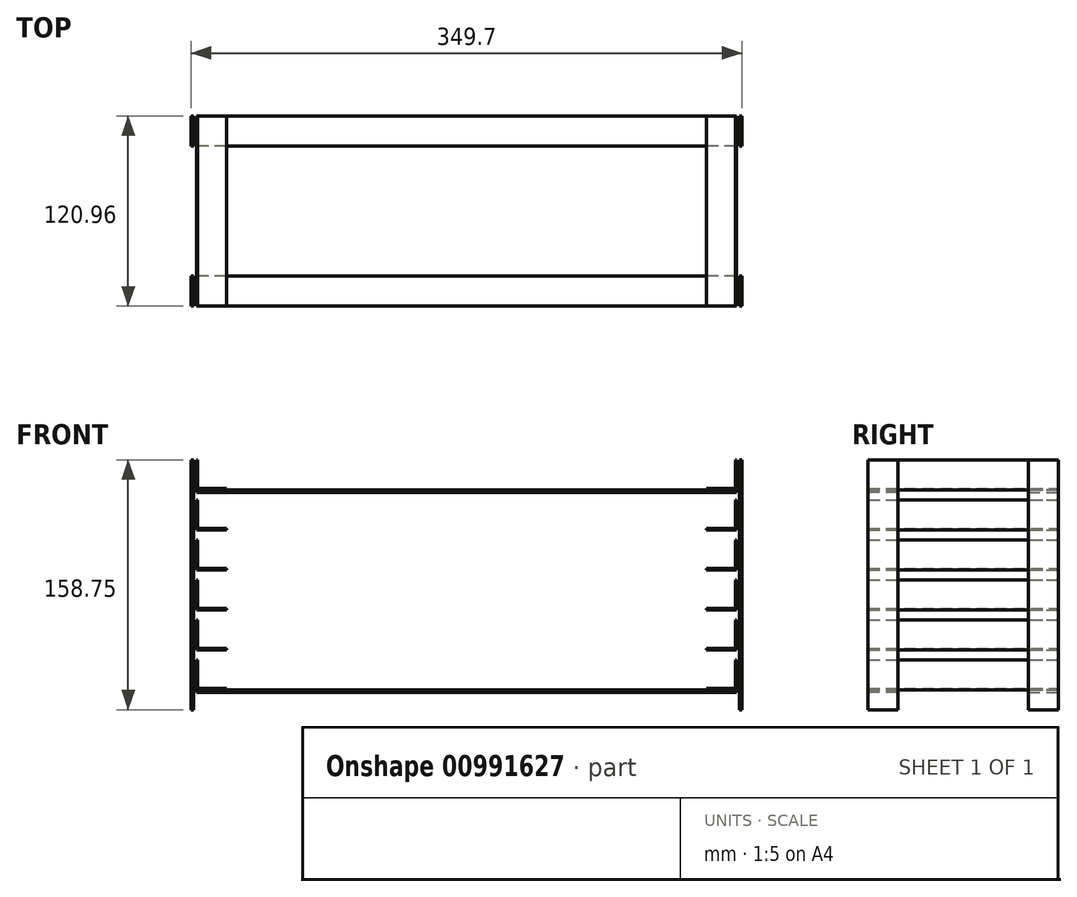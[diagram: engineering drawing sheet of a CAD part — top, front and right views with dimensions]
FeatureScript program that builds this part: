
annotation { "Feature Type Name" : "Feature", "Feature Type Description" : "" }
export const myFeature = defineFeature(function(context is Context, id is Id, definition is map)
    precondition{}
    {
        {
            var Q0;
            Q0=qCreatedBy(makeId("Front.planeOp"),FACE);
            var sketch = newSketch(context, id + "F0", { "sketchPlane" : qUnion([Q0])});
            skLineSegment(sketch, "E0", {"start": v(-171.45, 19.05) * mm, "end": v(-171.45, 0) * mm});
            skLineSegment(sketch, "E1", {"start": v(-171.45, 0) * mm, "end": v(-152.4, 0) * mm});
            skLineSegment(sketch, "E2", {"start": v(-152.4, 0) * mm, "end": v(-152.4, 0.76) * mm});
            skLineSegment(sketch, "E3", {"start": v(-152.4, 0.76) * mm, "end": v(-170.69, 0.76) * mm});
            skLineSegment(sketch, "E4", {"start": v(-171.45, 19.05) * mm, "end": v(-170.69, 19.05) * mm});
            skLineSegment(sketch, "E5", {"start": v(-170.69, 19.05) * mm, "end": v(-170.69, 0.76) * mm});
            skLineSegment(sketch, "E6.MirrorCS", {"start": v(152.4, 0.76) * mm, "end": v(170.69, 0.76) * mm});
            skLineSegment(sketch, "E7.MirrorCS", {"start": v(171.45, 0) * mm, "end": v(152.4, 0) * mm});
            skLineSegment(sketch, "E8.MirrorCS", {"start": v(170.69, 19.05) * mm, "end": v(170.69, 0.76) * mm});
            skLineSegment(sketch, "E9.MirrorCS", {"start": v(171.45, 19.05) * mm, "end": v(171.45, 0) * mm});
            skLineSegment(sketch, "E10.MirrorCS", {"start": v(171.45, 19.05) * mm, "end": v(170.69, 19.05) * mm});
            skLineSegment(sketch, "E11.MirrorCS", {"start": v(152.4, 0) * mm, "end": v(152.4, 0.76) * mm});
            skSolve(sketch);
        }
        {
            var Q0;
            Q0 = qSketchRegion(id + "F0", true);
            extrude(context, id + "F1", {"entities" : qUnion([Q0]), "endBound" : BoundingType.SYMMETRIC, "depth" : 120.65 * mm, "offsetDistance" : 25.4 * mm});
        }
        {
            var Q0;
            Q0=makeQuery(id+"F1.opExtrude","SWEPT_BODY",BODY,{"disambiguationData":[OSD([sQuery(id+"F0.wireOp",EDGE,"E0"),sQuery(id+"F0.wireOp",EDGE,"E1"),sQuery(id+"F0.wireOp",EDGE,"E2"),sQuery(id+"F0.wireOp",EDGE,"E3"),sQuery(id+"F0.wireOp",EDGE,"E4"),sQuery(id+"F0.wireOp",EDGE,"E5")])]});
            transform(context, id + "F2", {"entities" : qUnion([Q0]), "transformType" : TransformType.TRANSLATION_3D, "dx" : 0 * mm, "dy" : 0 * mm, "dz" : -25.4 * mm, "makeCopy" : true});
        }
        {
            var Q0;
            Q0=makeQuery(id+"F2.opPattern","COPY",BODY,{"derivedFrom":makeQuery(id+"F1.opExtrude","SWEPT_BODY",BODY,{"disambiguationData":[OSD([sQuery(id+"F0.wireOp",EDGE,"E0"),sQuery(id+"F0.wireOp",EDGE,"E1"),sQuery(id+"F0.wireOp",EDGE,"E2"),sQuery(id+"F0.wireOp",EDGE,"E3"),sQuery(id+"F0.wireOp",EDGE,"E4"),sQuery(id+"F0.wireOp",EDGE,"E5")])]}),"instanceName":"1"});
            transform(context, id + "F3", {"entities" : qUnion([Q0]), "transformType" : TransformType.TRANSLATION_3D, "dx" : 0 * mm, "dy" : 0 * mm, "dz" : -25.4 * mm, "makeCopy" : true});
        }
        {
            var Q0;
            Q0=makeQuery(id+"F3.opPattern","COPY",BODY,{"derivedFrom":makeQuery(id+"F2.opPattern","COPY",BODY,{"derivedFrom":makeQuery(id+"F1.opExtrude","SWEPT_BODY",BODY,{"disambiguationData":[OSD([sQuery(id+"F0.wireOp",EDGE,"E0"),sQuery(id+"F0.wireOp",EDGE,"E1"),sQuery(id+"F0.wireOp",EDGE,"E2"),sQuery(id+"F0.wireOp",EDGE,"E3"),sQuery(id+"F0.wireOp",EDGE,"E4"),sQuery(id+"F0.wireOp",EDGE,"E5")])]}),"instanceName":"1"}),"instanceName":"1"});
            transform(context, id + "F4", {"entities" : qUnion([Q0]), "transformType" : TransformType.TRANSLATION_3D, "dx" : 0 * mm, "dy" : 0 * mm, "dz" : -25.4 * mm, "makeCopy" : true});
        }
        {
            var Q0;
            Q0=makeQuery(id+"F4.opPattern","COPY",BODY,{"derivedFrom":makeQuery(id+"F3.opPattern","COPY",BODY,{"derivedFrom":makeQuery(id+"F2.opPattern","COPY",BODY,{"derivedFrom":makeQuery(id+"F1.opExtrude","SWEPT_BODY",BODY,{"disambiguationData":[OSD([sQuery(id+"F0.wireOp",EDGE,"E0"),sQuery(id+"F0.wireOp",EDGE,"E1"),sQuery(id+"F0.wireOp",EDGE,"E2"),sQuery(id+"F0.wireOp",EDGE,"E3"),sQuery(id+"F0.wireOp",EDGE,"E4"),sQuery(id+"F0.wireOp",EDGE,"E5")])]}),"instanceName":"1"}),"instanceName":"1"}),"instanceName":"1"});
            transform(context, id + "F5", {"entities" : qUnion([Q0]), "transformType" : TransformType.TRANSLATION_3D, "dx" : 0 * mm, "dy" : 0 * mm, "dz" : -25.4 * mm, "makeCopy" : true});
        }
        {
            var Q0;
            Q0=makeQuery(id+"F5.opPattern","COPY",BODY,{"derivedFrom":makeQuery(id+"F4.opPattern","COPY",BODY,{"derivedFrom":makeQuery(id+"F3.opPattern","COPY",BODY,{"derivedFrom":makeQuery(id+"F2.opPattern","COPY",BODY,{"derivedFrom":makeQuery(id+"F1.opExtrude","SWEPT_BODY",BODY,{"disambiguationData":[OSD([sQuery(id+"F0.wireOp",EDGE,"E0"),sQuery(id+"F0.wireOp",EDGE,"E1"),sQuery(id+"F0.wireOp",EDGE,"E2"),sQuery(id+"F0.wireOp",EDGE,"E3"),sQuery(id+"F0.wireOp",EDGE,"E4"),sQuery(id+"F0.wireOp",EDGE,"E5")])]}),"instanceName":"1"}),"instanceName":"1"}),"instanceName":"1"}),"instanceName":"1"});
            transform(context, id + "F6", {"entities" : qUnion([Q0]), "transformType" : TransformType.TRANSLATION_3D, "dx" : 0 * mm, "dy" : 0 * mm, "dz" : -25.4 * mm, "makeCopy" : true});
        }
        {
            var Q0;
            Q0=makeQuery(id+"F1.opExtrude","SWEPT_BODY",BODY,{"disambiguationData":[OSD([sQuery(id+"F0.wireOp",EDGE,"E6.MirrorCS"),sQuery(id+"F0.wireOp",EDGE,"E8.MirrorCS"),sQuery(id+"F0.wireOp",EDGE,"E7.MirrorCS"),sQuery(id+"F0.wireOp",EDGE,"E9.MirrorCS"),sQuery(id+"F0.wireOp",EDGE,"E10.MirrorCS"),sQuery(id+"F0.wireOp",EDGE,"E11.MirrorCS")])]});
            transform(context, id + "F7", {"entities" : qUnion([Q0]), "transformType" : TransformType.TRANSLATION_3D, "dx" : 0 * mm, "dy" : 0 * mm, "dz" : -25.4 * mm, "makeCopy" : true});
        }
        {
            var Q0;
            Q0=makeQuery(id+"F7.opPattern","COPY",BODY,{"derivedFrom":makeQuery(id+"F1.opExtrude","SWEPT_BODY",BODY,{"disambiguationData":[OSD([sQuery(id+"F0.wireOp",EDGE,"E6.MirrorCS"),sQuery(id+"F0.wireOp",EDGE,"E8.MirrorCS"),sQuery(id+"F0.wireOp",EDGE,"E7.MirrorCS"),sQuery(id+"F0.wireOp",EDGE,"E9.MirrorCS"),sQuery(id+"F0.wireOp",EDGE,"E10.MirrorCS"),sQuery(id+"F0.wireOp",EDGE,"E11.MirrorCS")])]}),"instanceName":"1"});
            transform(context, id + "F8", {"entities" : qUnion([Q0]), "transformType" : TransformType.TRANSLATION_3D, "dx" : 0 * mm, "dy" : 0 * mm, "dz" : -25.4 * mm, "makeCopy" : true});
        }
        {
            var Q0;
            Q0=makeQuery(id+"F8.opPattern","COPY",BODY,{"derivedFrom":makeQuery(id+"F7.opPattern","COPY",BODY,{"derivedFrom":makeQuery(id+"F1.opExtrude","SWEPT_BODY",BODY,{"disambiguationData":[OSD([sQuery(id+"F0.wireOp",EDGE,"E6.MirrorCS"),sQuery(id+"F0.wireOp",EDGE,"E8.MirrorCS"),sQuery(id+"F0.wireOp",EDGE,"E7.MirrorCS"),sQuery(id+"F0.wireOp",EDGE,"E9.MirrorCS"),sQuery(id+"F0.wireOp",EDGE,"E10.MirrorCS"),sQuery(id+"F0.wireOp",EDGE,"E11.MirrorCS")])]}),"instanceName":"1"}),"instanceName":"1"});
            transform(context, id + "F9", {"entities" : qUnion([Q0]), "transformType" : TransformType.TRANSLATION_3D, "dx" : 0 * mm, "dy" : 0 * mm, "dz" : -25.4 * mm, "makeCopy" : true});
        }
        {
            var Q0;
            Q0=makeQuery(id+"F9.opPattern","COPY",BODY,{"derivedFrom":makeQuery(id+"F8.opPattern","COPY",BODY,{"derivedFrom":makeQuery(id+"F7.opPattern","COPY",BODY,{"derivedFrom":makeQuery(id+"F1.opExtrude","SWEPT_BODY",BODY,{"disambiguationData":[OSD([sQuery(id+"F0.wireOp",EDGE,"E6.MirrorCS"),sQuery(id+"F0.wireOp",EDGE,"E8.MirrorCS"),sQuery(id+"F0.wireOp",EDGE,"E7.MirrorCS"),sQuery(id+"F0.wireOp",EDGE,"E9.MirrorCS"),sQuery(id+"F0.wireOp",EDGE,"E10.MirrorCS"),sQuery(id+"F0.wireOp",EDGE,"E11.MirrorCS")])]}),"instanceName":"1"}),"instanceName":"1"}),"instanceName":"1"});
            transform(context, id + "F10", {"entities" : qUnion([Q0]), "transformType" : TransformType.TRANSLATION_3D, "dx" : 0 * mm, "dy" : 0 * mm, "dz" : -25.4 * mm, "makeCopy" : true});
        }
        {
            var Q0;
            Q0=makeQuery(id+"F10.opPattern","COPY",BODY,{"derivedFrom":makeQuery(id+"F9.opPattern","COPY",BODY,{"derivedFrom":makeQuery(id+"F8.opPattern","COPY",BODY,{"derivedFrom":makeQuery(id+"F7.opPattern","COPY",BODY,{"derivedFrom":makeQuery(id+"F1.opExtrude","SWEPT_BODY",BODY,{"disambiguationData":[OSD([sQuery(id+"F0.wireOp",EDGE,"E6.MirrorCS"),sQuery(id+"F0.wireOp",EDGE,"E8.MirrorCS"),sQuery(id+"F0.wireOp",EDGE,"E7.MirrorCS"),sQuery(id+"F0.wireOp",EDGE,"E9.MirrorCS"),sQuery(id+"F0.wireOp",EDGE,"E10.MirrorCS"),sQuery(id+"F0.wireOp",EDGE,"E11.MirrorCS")])]}),"instanceName":"1"}),"instanceName":"1"}),"instanceName":"1"}),"instanceName":"1"});
            transform(context, id + "F11", {"entities" : qUnion([Q0]), "transformType" : TransformType.TRANSLATION_3D, "dx" : 0 * mm, "dy" : 0 * mm, "dz" : -25.4 * mm, "makeCopy" : true});
        }
        {
            var Q0;
            Q0=qCreatedBy(makeId("Top.planeOp"),FACE);
            var sketch = newSketch(context, id + "F12", { "sketchPlane" : qUnion([Q0])});
            skLineSegment(sketch, "E12", {"start": v(173.26, 60.47) * mm, "end": v(173.26, 41.42) * mm});
            skLineSegment(sketch, "E13", {"start": v(173.26, 60.47) * mm, "end": v(174.85, 60.47) * mm});
            skLineSegment(sketch, "E14", {"start": v(174.85, 60.47) * mm, "end": v(174.85, 41.42) * mm});
            skLineSegment(sketch, "E15", {"start": v(174.85, 41.42) * mm, "end": v(173.26, 41.42) * mm});
            skLineSegment(sketch, "E16.MirrorCS", {"start": v(174.85, -60.47) * mm, "end": v(174.85, -41.42) * mm});
            skLineSegment(sketch, "E17.MirrorCS", {"start": v(173.26, -60.47) * mm, "end": v(173.26, -41.42) * mm});
            skLineSegment(sketch, "E18.MirrorCS", {"start": v(173.26, -60.47) * mm, "end": v(174.85, -60.47) * mm});
            skLineSegment(sketch, "E19.MirrorCS", {"start": v(174.85, -41.42) * mm, "end": v(173.26, -41.42) * mm});
            skLineSegment(sketch, "E20.MirrorCS", {"start": v(-173.26, -60.47) * mm, "end": v(-174.85, -60.47) * mm});
            skLineSegment(sketch, "E21.MirrorCS", {"start": v(-173.26, -60.47) * mm, "end": v(-173.26, -41.42) * mm});
            skLineSegment(sketch, "E22.MirrorCS", {"start": v(-174.85, -60.47) * mm, "end": v(-174.85, -41.42) * mm});
            skLineSegment(sketch, "E23.MirrorCS", {"start": v(-174.85, 41.42) * mm, "end": v(-173.26, 41.42) * mm});
            skLineSegment(sketch, "E24.MirrorCS", {"start": v(-174.85, 60.47) * mm, "end": v(-174.85, 41.42) * mm});
            skLineSegment(sketch, "E25.MirrorCS", {"start": v(-173.26, 60.47) * mm, "end": v(-174.85, 60.47) * mm});
            skLineSegment(sketch, "E26.MirrorCS", {"start": v(-173.26, 60.47) * mm, "end": v(-173.26, 41.42) * mm});
            skLineSegment(sketch, "E27.MirrorCS", {"start": v(-174.85, -41.42) * mm, "end": v(-173.26, -41.42) * mm});
            skSolve(sketch);
        }
        {
            var Q0;
            Q0 = qSketchRegion(id + "F12", true);
            extrude(context, id + "F13", {"entities" : qUnion([Q0]), "depth" : 19.05 * mm, "offsetDistance" : 25.4 * mm, "hasSecondDirection" : true, "secondDirectionOppositeDirection" : true, "secondDirectionDepth" : 139.7 * mm});
        }
        {
            var Q0;
            Q0=qCreatedBy(makeId("Right.planeOp"),FACE);
            var sketch = newSketch(context, id + "F14", { "sketchPlane" : qUnion([Q0])});
            skLineSegment(sketch, "E28", {"start": v(-60.48, -127.12) * mm, "end": v(-60.48, -128.7) * mm});
            skLineSegment(sketch, "E29", {"start": v(-60.48, -127.12) * mm, "end": v(-41.43, -127.12) * mm});
            skLineSegment(sketch, "E30", {"start": v(-41.43, -127.12) * mm, "end": v(-41.43, -128.7) * mm});
            skLineSegment(sketch, "E31", {"start": v(-41.43, -128.7) * mm, "end": v(-60.48, -128.7) * mm});
            skLineSegment(sketch, "E32.MirrorCS", {"start": v(60.48, -127.12) * mm, "end": v(60.48, -128.7) * mm});
            skLineSegment(sketch, "E33.MirrorCS", {"start": v(60.48, -127.12) * mm, "end": v(41.43, -127.12) * mm});
            skLineSegment(sketch, "E34.MirrorCS", {"start": v(41.43, -127.12) * mm, "end": v(41.43, -128.7) * mm});
            skLineSegment(sketch, "E35.MirrorCS", {"start": v(41.43, -128.7) * mm, "end": v(60.48, -128.7) * mm});
            skLineSegment(sketch, "E36", {"start": v(-60.47, 0) * mm, "end": v(-60.47, -1.59) * mm});
            skLineSegment(sketch, "E37", {"start": v(-60.47, 0) * mm, "end": v(-41.42, 0) * mm});
            skLineSegment(sketch, "E38", {"start": v(-41.42, 0) * mm, "end": v(-41.42, -1.59) * mm});
            skLineSegment(sketch, "E39", {"start": v(-41.42, -1.59) * mm, "end": v(-60.47, -1.59) * mm});
            skLineSegment(sketch, "E40.MirrorCS", {"start": v(60.47, 0) * mm, "end": v(41.42, 0) * mm});
            skLineSegment(sketch, "E41.MirrorCS", {"start": v(41.42, -1.59) * mm, "end": v(60.47, -1.59) * mm});
            skLineSegment(sketch, "E42.MirrorCS", {"start": v(60.47, 0) * mm, "end": v(60.47, -1.59) * mm});
            skLineSegment(sketch, "E43.MirrorCS", {"start": v(41.42, 0) * mm, "end": v(41.42, -1.59) * mm});
            skSolve(sketch);
        }
        {
            var Q0;
            Q0 = qSketchRegion(id + "F14", true);
            extrude(context, id + "F15", {"entities" : qUnion([Q0]), "depth" : 171.45 * mm, "offsetDistance" : 25.4 * mm, "hasSecondDirection" : true, "secondDirectionOppositeDirection" : true, "secondDirectionDepth" : 171.45 * mm});
        }
    });
